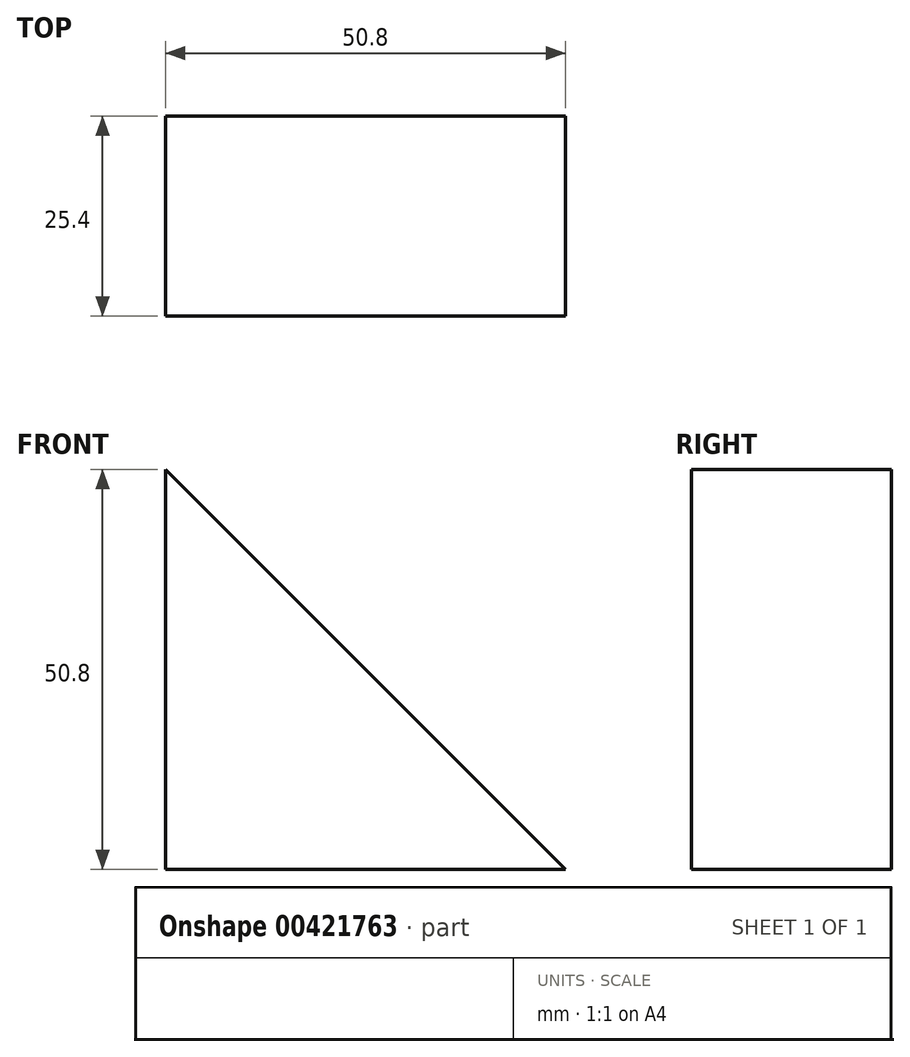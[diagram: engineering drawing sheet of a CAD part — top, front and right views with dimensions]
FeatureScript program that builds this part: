
annotation { "Feature Type Name" : "Feature", "Feature Type Description" : "" }
export const myFeature = defineFeature(function(context is Context, id is Id, definition is map)
    precondition{}
    {
        {
            var Q0;
            Q0=qCreatedBy(makeId("Front.planeOp"),FACE);
            var sketch = newSketch(context, id + "F0", { "sketchPlane" : qUnion([Q0])});
            skLineSegment(sketch, "E0", {"start": v(0, 0) * mm, "end": v(-50.8, 0) * mm});
            skLineSegment(sketch, "E1", {"start": v(-50.8, 0) * mm, "end": v(-50.8, 50.8) * mm});
            skLineSegment(sketch, "E2", {"start": v(-50.8, 50.8) * mm, "end": v(0, 0) * mm});
            skSolve(sketch);
        }
        {
            var Q0;
            Q0 = qSketchRegion(id + "F0", true);
            extrude(context, id + "F1", {"entities" : qUnion([Q0]), "depth" : 25.4 * mm});
        }
    });
